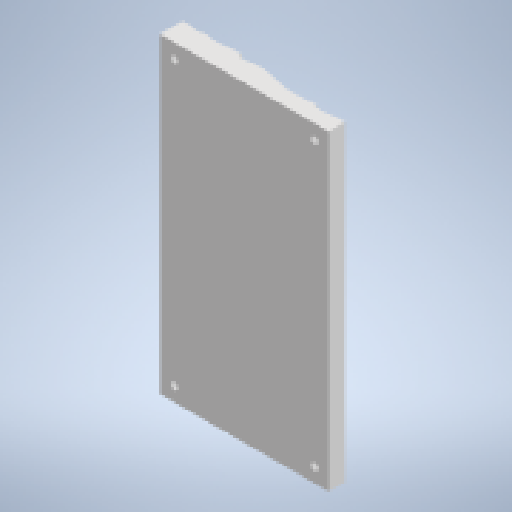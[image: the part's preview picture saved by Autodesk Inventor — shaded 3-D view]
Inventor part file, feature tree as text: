
AUTODESK INVENTOR PART (.ipt)
format: ipt  version: 2023 (Build 270158000, 158)  size: 271,360 bytes
history: native  units: mm
features: reference x10, other x7, extrude x3, sketch x2
ambient origin geometry x8: Origin, YZ Plane, XZ Plane, XY Plane, X Axis, Y Axis, Z Axis, Center Point
bodies: Solid1 (feature_tree)
feature tree (22):
  extrude  "Extrusion1"  Depth=1.0mm
  extrude  "Extrusion5"  Depth=10.0mm
  extrude  "Extrusion6"  Depth=4.0mm TaperAngle=0.0deg
  sketch  "Sketch1"  dims[d3=5.0mm d4=9.75mm d5=0.0mm d6=0.0mm d8=1.0mm]
  reference  "Reference1"
  reference  "Reference2"
  reference  "Reference3"
  reference  "Reference4"
  reference  "Reference5"
  reference  "Reference8"
  sketch  "Sketch6"  dims[d19=202.5mm d20=0.0mm d21=10.0mm d22=4.0mm d23=0.0mm d24=0.872665mm]
  reference  "Reference9"
  reference  "Reference10"
  reference  "Reference11"
  reference  "Reference12"
  parser-record x1  (decoder bookkeeping rows leaked as tree rows — omitted from the tree; the rows remain in map.json)
  other  "doorLockAssembly_V4.iam"
  other  "moulding:1"
  other  "rack_V3:1"
  other  "gear_V4:1"
  other  "BallBearing_8x22x7mm:1"
  other  "housingFront:1"
note: 1 file-system path scrubbed to <path> (originals preserved in map.json)
